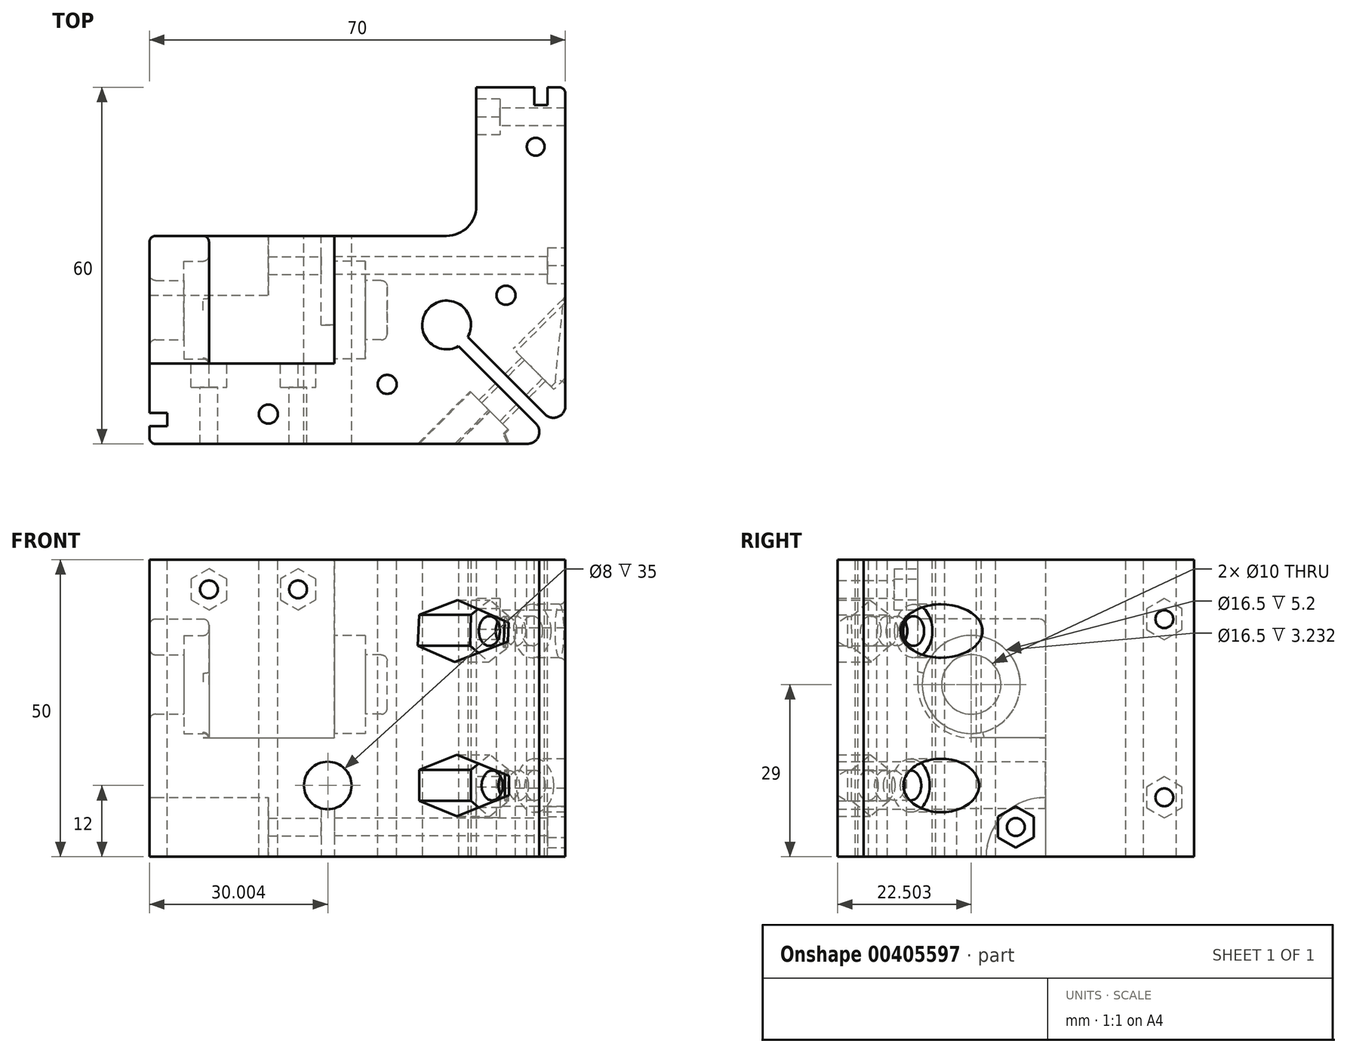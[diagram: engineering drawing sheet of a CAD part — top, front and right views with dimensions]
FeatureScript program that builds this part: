
annotation { "Feature Type Name" : "Feature", "Feature Type Description" : "" }
export const myFeature = defineFeature(function(context is Context, id is Id, definition is map)
    precondition{}
    {
        {
            var Q0;
            Q0=qCreatedBy(makeId("Top.planeOp"),FACE);
            var sketch = newSketch(context, id + "F0", { "sketchPlane" : qUnion([Q0])});
            skLineSegment(sketch, "E0.bottom", {"start": v(-61.79, 60.93) * mm, "end": v(-1.79, 60.93) * mm});
            skLineSegment(sketch, "E0.top", {"start": v(-61.79, 0.93) * mm, "end": v(-4.07, 0.93) * mm});
            skLineSegment(sketch, "E0.left", {"start": v(-61.79, 60.93) * mm, "end": v(-61.79, 0.93) * mm});
            skLineSegment(sketch, "E0.right", {"start": v(-1.79, 60.93) * mm, "end": v(-1.79, 3.21) * mm});
            skLineSegment(sketch, "E1", {"start": v(-18.22, 18.92) * mm, "end": v(-2.3, 3) * mm});
            skLineSegment(sketch, "E2.MirrorCS", {"start": v(-19.77, 17.36) * mm, "end": v(-3.85, 1.44) * mm});
            skPoint(sketch, "E3.visualSharp", {"position": v(-1.79, 2.49) * mm});
            skPoint(sketch, "E4.visualSharp", {"position": v(-3.34, 0.93) * mm});
            skArc(sketch, "E5", {"start": v(-18.22, 18.92) * mm, "mid": v(-24.69, 23.83) * mm, "end": v(-19.77, 17.36) * mm});
            skLineSegment(sketch, "E6", {"start": v(-3.85, 1.44) * mm, "end": v(-3.34, 0.93) * mm});
            skLineSegment(sketch, "E7", {"start": v(-2.3, 3) * mm, "end": v(-1.79, 2.49) * mm});
            skLineSegment(sketch, "E8", {"start": v(-1.79, 3.21) * mm, "end": v(-1.79, 2.49) * mm});
            skLineSegment(sketch, "E9", {"start": v(-3.34, 0.93) * mm, "end": v(-4.07, 0.93) * mm});
            skSolve(sketch);
        }
        {
            var Q0;
            Q0=qSketchRegion(id+"F0",true);
            extrude(context, id + "F1", {"entities" : qUnion([Q0]), "depth" : 50 * mm});
        }
        {
            var Q0;
            Q0=makeQuery(id+"F1.opExtrude","SWEPT_FACE",FACE,{"disambiguationData":[OSD([sQuery(id+"F0.wireOp",EDGE,"E1")])]});
            var sketch = newSketch(context, id + "F2", { "sketchPlane" : qUnion([Q0])});
            skCircle(sketch, "E10", {"center": v(-14.26, 12) * mm, "radius": 2.5 * mm});
            skCircle(sketch, "E11", {"center": v(-14.92, 38) * mm, "radius": 4.5 * mm});
            skCircle(sketch, "E12", {"center": v(-14.26, 12) * mm, "radius": 4.5 * mm});
            skCircle(sketch, "E13", {"center": v(-14.92, 38) * mm, "radius": 2.5 * mm});
            skCircle(sketch, "E14.cCircle", {"center": v(-14.92, 38) * mm, "radius": 4.5 * mm, "construction": true});
            skLineSegment(sketch, "E14.0", {"start": v(-10.5, 35.26) * mm, "end": v(-15.08, 32.8) * mm});
            skLineSegment(sketch, "E14.1", {"start": v(-15.08, 32.8) * mm, "end": v(-19.5, 35.54) * mm});
            skLineSegment(sketch, "E14.2", {"start": v(-19.5, 35.54) * mm, "end": v(-19.34, 40.74) * mm});
            skLineSegment(sketch, "E14.3", {"start": v(-19.34, 40.74) * mm, "end": v(-14.76, 43.2) * mm});
            skLineSegment(sketch, "E14.4", {"start": v(-14.76, 43.2) * mm, "end": v(-10.34, 40.46) * mm});
            skLineSegment(sketch, "E14.5", {"start": v(-10.34, 40.46) * mm, "end": v(-10.5, 35.26) * mm});
            skPoint(sketch, "E14.0.midPoint", {"position": v(-12.79, 34.04) * mm});
            skSolve(sketch);
        }
        {
            var Q0;
            Q0=sQuery(id+"F2.wireOp",VERTEX,"E11.center");
            var Q1;
            Q1=makeQuery(id+"F1.opExtrude","SWEPT_BODY",BODY,{"disambiguationData":[OSD([sQuery(id+"F0.wireOp",EDGE,"E0.bottom"),sQuery(id+"F0.wireOp",EDGE,"E0.top"),sQuery(id+"F0.wireOp",EDGE,"E0.left"),sQuery(id+"F0.wireOp",EDGE,"E0.right"),sQuery(id+"F0.wireOp",EDGE,"qFsGaKan-yORc-CTVH-xqod-amC7XaK1J5uG"),sQuery(id+"F0.wireOp",EDGE,"E1"),sQuery(id+"F0.wireOp",EDGE,"E2.MirrorCS"),sQuery(id+"F0.wireOp",EDGE,"cd217c19-c853-48cb-b8bd-9b78fb10cb74.filletArc"),sQuery(id+"F0.wireOp",EDGE,"a7c015ec-a513-4ea6-9d75-b2fe8166aac2.filletArc"),sQuery(id+"F0.wireOp",EDGE,"E3.filletArc"),sQuery(id+"F0.wireOp",EDGE,"E4.filletArc")])]});
            hole(context, id + "F3", {"style" : HoleStyle.SIMPLE, "endStyle" : HoleEndStyle.THROUGH, "holeDiameter" : 5 * mm, "isTappedThrough" : true, "tappedDepth" : 12 * mm, "tapClearance" : 3, "locations" : qUnion([Q0]), "scope" : qUnion([Q1])});
        }
        {
            var Q0;
            Q0=sQuery(id+"F2.wireOp",VERTEX,"E11.center");
            var Q1;
            Q1=makeQuery(id+"F1.opExtrude","SWEPT_BODY",BODY,{"disambiguationData":[OSD([sQuery(id+"F0.wireOp",EDGE,"E0.bottom"),sQuery(id+"F0.wireOp",EDGE,"E0.top"),sQuery(id+"F0.wireOp",EDGE,"E0.left"),sQuery(id+"F0.wireOp",EDGE,"E0.right"),sQuery(id+"F0.wireOp",EDGE,"qFsGaKan-yORc-CTVH-xqod-amC7XaK1J5uG"),sQuery(id+"F0.wireOp",EDGE,"E1"),sQuery(id+"F0.wireOp",EDGE,"E2.MirrorCS"),sQuery(id+"F0.wireOp",EDGE,"cd217c19-c853-48cb-b8bd-9b78fb10cb74.filletArc"),sQuery(id+"F0.wireOp",EDGE,"a7c015ec-a513-4ea6-9d75-b2fe8166aac2.filletArc"),sQuery(id+"F0.wireOp",EDGE,"E3.filletArc"),sQuery(id+"F0.wireOp",EDGE,"E4.filletArc")])]});
            hole(context, id + "F4", {"style" : HoleStyle.SIMPLE, "endStyle" : HoleEndStyle.THROUGH, "oppositeDirection" : true, "standardTappedOrClearance" : lookupTablePath({ "standard" : "自訂" }), "standardBlindInLast" : lookupTablePath({ "standard" : "自訂" }), "holeDiameter" : 5 * mm, "isTappedThrough" : true, "tappedDepth" : 12 * mm, "tapClearance" : 3, "locations" : qUnion([Q0]), "scope" : qUnion([Q1])});
        }
        {
            var Q0;
            Q0=makeQuery(id+"F2.imprint","IMPRINT",FACE,{"disambiguationData":[TD([[makeQuery(id+"F2.imprint","IMPRINT",EDGE,{"derivedFrom":sQuery(id+"F2.wireOp",EDGE,"E11")}),1.0]])]});
            var Q1;
            Q1=sQuery(id+"F2.wireOp",EDGE,"E11");
            extrude(context, id + "F5", {"entities" : qUnion([Q0]), "surfaceEntities" : qUnion([Q1]), "oppositeDirection" : true, "depth" : 25 * mm});
        }
        {
            var Q0;
            Q0=makeQuery(id+"F5.opExtrude","SWEPT_BODY",BODY,{"disambiguationData":[OSD([sQuery(id+"F2.wireOp",EDGE,"E11"),sQuery(id+"F2.wireOp",EDGE,"E13")])]});
            var Q1;
            Q1=makeQuery(id+"F1.opExtrude","SWEPT_BODY",BODY,{"disambiguationData":[OSD([sQuery(id+"F0.wireOp",EDGE,"E0.bottom"),sQuery(id+"F0.wireOp",EDGE,"E0.top"),sQuery(id+"F0.wireOp",EDGE,"E0.left"),sQuery(id+"F0.wireOp",EDGE,"E0.right"),sQuery(id+"F0.wireOp",EDGE,"qFsGaKan-yORc-CTVH-xqod-amC7XaK1J5uG"),sQuery(id+"F0.wireOp",EDGE,"E1"),sQuery(id+"F0.wireOp",EDGE,"E2.MirrorCS"),sQuery(id+"F0.wireOp",EDGE,"cd217c19-c853-48cb-b8bd-9b78fb10cb74.filletArc"),sQuery(id+"F0.wireOp",EDGE,"a7c015ec-a513-4ea6-9d75-b2fe8166aac2.filletArc"),sQuery(id+"F0.wireOp",EDGE,"E3.filletArc"),sQuery(id+"F0.wireOp",EDGE,"E4.filletArc")])]});
            booleanBodies(context, id + "F6", {"operationType" : BooleanOperationType.SUBTRACTION, "tools" : qUnion([Q0]), "targets" : qUnion([Q1])});
        }
        {
            var Q0;
            Q0=makeQuery(id+"F2.imprint","IMPRINT",FACE,{"disambiguationData":[TD([[makeQuery(id+"F2.imprint","IMPRINT",EDGE,{"derivedFrom":sQuery(id+"F2.wireOp",EDGE,"E11")}),1.0]])]});
            extrude(context, id + "F7", {"entities" : qUnion([Q0]), "operationType" : NewBodyOperationType.ADD, "oppositeDirection" : true, "depth" : 4 * mm});
        }
        {
            var Q0;
            Q0=sQuery(id+"F2.wireOp",VERTEX,"E10.center");
            var Q1;
            Q1=makeQuery(id+"F1.opExtrude","SWEPT_BODY",BODY,{"disambiguationData":[OSD([sQuery(id+"F0.wireOp",EDGE,"E0.bottom"),sQuery(id+"F0.wireOp",EDGE,"E0.top"),sQuery(id+"F0.wireOp",EDGE,"E0.left"),sQuery(id+"F0.wireOp",EDGE,"E0.right"),sQuery(id+"F0.wireOp",EDGE,"qFsGaKan-yORc-CTVH-xqod-amC7XaK1J5uG"),sQuery(id+"F0.wireOp",EDGE,"E1"),sQuery(id+"F0.wireOp",EDGE,"E2.MirrorCS"),sQuery(id+"F0.wireOp",EDGE,"cd217c19-c853-48cb-b8bd-9b78fb10cb74.filletArc"),sQuery(id+"F0.wireOp",EDGE,"a7c015ec-a513-4ea6-9d75-b2fe8166aac2.filletArc"),sQuery(id+"F0.wireOp",EDGE,"E3.filletArc"),sQuery(id+"F0.wireOp",EDGE,"E4.filletArc")])]});
            hole(context, id + "F8", {"style" : HoleStyle.SIMPLE, "endStyle" : HoleEndStyle.THROUGH, "oppositeDirection" : true, "standardTappedOrClearance" : lookupTablePath({ "standard" : "自訂" }), "standardBlindInLast" : lookupTablePath({ "standard" : "自訂" }), "holeDiameter" : 5 * mm, "isTappedThrough" : true, "tappedDepth" : 12 * mm, "tapClearance" : 3, "locations" : qUnion([Q0]), "scope" : qUnion([Q1])});
        }
        {
            var Q0;
            Q0=makeQuery(id+"F1.opExtrude","SWEPT_FACE",FACE,{"disambiguationData":[OSD([sQuery(id+"F0.wireOp",EDGE,"E2.MirrorCS")])]});
            var sketch = newSketch(context, id + "F9", { "sketchPlane" : qUnion([Q0])});
            skCircle(sketch, "E15.cCircle", {"center": v(14.92, 38) * mm, "radius": 4.5 * mm, "construction": true});
            skLineSegment(sketch, "E15.0", {"start": v(10.34, 40.45) * mm, "end": v(14.75, 43.2) * mm});
            skLineSegment(sketch, "E15.1", {"start": v(14.75, 43.2) * mm, "end": v(19.33, 40.74) * mm});
            skLineSegment(sketch, "E15.2", {"start": v(19.33, 40.74) * mm, "end": v(19.5, 35.55) * mm});
            skLineSegment(sketch, "E15.3", {"start": v(19.5, 35.55) * mm, "end": v(15.08, 32.8) * mm});
            skLineSegment(sketch, "E15.4", {"start": v(15.08, 32.8) * mm, "end": v(10.5, 35.26) * mm});
            skLineSegment(sketch, "E15.5", {"start": v(10.5, 35.26) * mm, "end": v(10.34, 40.45) * mm});
            skPoint(sketch, "E15.0.midPoint", {"position": v(12.54, 41.82) * mm});
            skCircle(sketch, "E16", {"center": v(14.92, 38) * mm, "radius": 2.5 * mm});
            skCircle(sketch, "E17.cCircle", {"center": v(14.82, 12) * mm, "radius": 4.5 * mm, "construction": true});
            skLineSegment(sketch, "E17.0", {"start": v(19.32, 14.6) * mm, "end": v(19.32, 9.4) * mm});
            skLineSegment(sketch, "E17.1", {"start": v(19.32, 9.4) * mm, "end": v(14.82, 6.8) * mm});
            skLineSegment(sketch, "E17.2", {"start": v(14.82, 6.8) * mm, "end": v(10.32, 9.4) * mm});
            skLineSegment(sketch, "E17.3", {"start": v(10.32, 9.4) * mm, "end": v(10.32, 14.6) * mm});
            skLineSegment(sketch, "E17.4", {"start": v(10.32, 14.6) * mm, "end": v(14.82, 17.2) * mm});
            skLineSegment(sketch, "E17.5", {"start": v(14.82, 17.2) * mm, "end": v(19.32, 14.6) * mm});
            skPoint(sketch, "E17.0.midPoint", {"position": v(19.32, 12) * mm});
            skSolve(sketch);
        }
        {
            var Q0;
            Q0=qSketchRegion(id+"F9",true);
            extrude(context, id + "F10", {"entities" : qUnion([Q0]), "operationType" : NewBodyOperationType.REMOVE, "oppositeDirection" : true, "depth" : 25 * mm});
        }
        {
            var Q0;
            Q0=makeQuery(id+"F9.imprint","IMPRINT",FACE,{"disambiguationData":[TD([[makeQuery(id+"F9.imprint","IMPRINT",EDGE,{"derivedFrom":sQuery(id+"F9.wireOp",EDGE,"E15.0")}),-1.0]])]});
            var Q1;
            Q1=sQuery(id+"F9.wireOp",EDGE,"E15.2");
            extrude(context, id + "F11", {"entities" : qUnion([Q0]), "operationType" : NewBodyOperationType.ADD, "surfaceEntities" : qUnion([Q1]), "oppositeDirection" : true, "depth" : 4 * mm});
        }
        {
            var Q0;
            Q0=sQuery(id+"F2.wireOp",VERTEX,"E10.center");
            var Q1;
            Q1=makeQuery(id+"F1.opExtrude","SWEPT_BODY",BODY,{"disambiguationData":[OSD([sQuery(id+"F0.wireOp",EDGE,"E0.bottom"),sQuery(id+"F0.wireOp",EDGE,"E0.top"),sQuery(id+"F0.wireOp",EDGE,"E0.left"),sQuery(id+"F0.wireOp",EDGE,"E0.right"),sQuery(id+"F0.wireOp",EDGE,"qFsGaKan-yORc-CTVH-xqod-amC7XaK1J5uG"),sQuery(id+"F0.wireOp",EDGE,"E1"),sQuery(id+"F0.wireOp",EDGE,"E2.MirrorCS"),sQuery(id+"F0.wireOp",EDGE,"cd217c19-c853-48cb-b8bd-9b78fb10cb74.filletArc"),sQuery(id+"F0.wireOp",EDGE,"a7c015ec-a513-4ea6-9d75-b2fe8166aac2.filletArc"),sQuery(id+"F0.wireOp",EDGE,"E3.filletArc"),sQuery(id+"F0.wireOp",EDGE,"E4.filletArc")])]});
            hole(context, id + "F12", {"style" : HoleStyle.SIMPLE, "endStyle" : HoleEndStyle.THROUGH, "standardTappedOrClearance" : lookupTablePath({ "standard" : "自訂" }), "standardBlindInLast" : lookupTablePath({ "standard" : "自訂" }), "holeDiameter" : 9 * mm, "isTappedThrough" : true, "tappedDepth" : 12 * mm, "tapClearance" : 3, "locations" : qUnion([Q0]), "scope" : qUnion([Q1])});
        }
        {
            var Q0;
            Q0=makeQuery(id+"F2.imprint","IMPRINT",FACE,{"disambiguationData":[TD([[makeQuery(id+"F2.imprint","IMPRINT",EDGE,{"derivedFrom":sQuery(id+"F2.wireOp",EDGE,"E10")}),-1.0]])]});
            extrude(context, id + "F13", {"entities" : qUnion([Q0]), "operationType" : NewBodyOperationType.ADD, "oppositeDirection" : true, "depth" : 4 * mm});
        }
        {
            var Q0;
            Q0=makeQuery(id+"F9.imprint","IMPRINT",FACE,{"disambiguationData":[TD([[makeQuery(id+"F9.imprint","IMPRINT",EDGE,{"derivedFrom":sQuery(id+"F9.wireOp",EDGE,"E17.0")}),-1.0]])]});
            extrude(context, id + "F14", {"entities" : qUnion([Q0]), "operationType" : NewBodyOperationType.ADD, "oppositeDirection" : true, "depth" : 4 * mm});
        }
        {
            var Q0;
            Q0=makeQuery(id+"F1.opExtrude","SWEPT_FACE",FACE,{"disambiguationData":[OSD([sQuery(id+"F0.wireOp",EDGE,"E0.bottom")])]});
            var sketch = newSketch(context, id + "F15", { "sketchPlane" : qUnion([Q0])});
            skCircle(sketch, "E18", {"center": v(41.79, 12) * mm, "radius": 1.1 * mm});
            skLineSegment(sketch, "E19", {"start": v(40.69, 50) * mm, "end": v(40.69, 0) * mm});
            skLineSegment(sketch, "E20.MirrorCS", {"start": v(42.89, 50) * mm, "end": v(42.89, 0) * mm});
            skLineSegment(sketch, "E21", {"start": v(16.79, 50) * mm, "end": v(16.79, 0) * mm});
            skLineSegment(sketch, "E22.bottom", {"start": v(40.69, 50) * mm, "end": v(42.89, 50) * mm});
            skLineSegment(sketch, "E22.left", {"start": v(40.69, 50) * mm, "end": v(40.69, 30) * mm});
            skSolve(sketch);
        }
        {
            var Q0;
            Q0=sQuery(id+"F15.wireOp",VERTEX,"E18.center");
            var Q1;
            Q1=makeQuery(id+"F1.opExtrude","SWEPT_BODY",BODY,{"disambiguationData":[OSD([sQuery(id+"F0.wireOp",EDGE,"E0.bottom"),sQuery(id+"F0.wireOp",EDGE,"E0.top"),sQuery(id+"F0.wireOp",EDGE,"E0.left"),sQuery(id+"F0.wireOp",EDGE,"E0.right"),sQuery(id+"F0.wireOp",EDGE,"qFsGaKan-yORc-CTVH-xqod-amC7XaK1J5uG"),sQuery(id+"F0.wireOp",EDGE,"E1"),sQuery(id+"F0.wireOp",EDGE,"E2.MirrorCS"),sQuery(id+"F0.wireOp",EDGE,"cd217c19-c853-48cb-b8bd-9b78fb10cb74.filletArc"),sQuery(id+"F0.wireOp",EDGE,"a7c015ec-a513-4ea6-9d75-b2fe8166aac2.filletArc"),sQuery(id+"F0.wireOp",EDGE,"E3.filletArc"),sQuery(id+"F0.wireOp",EDGE,"E4.filletArc")])]});
            hole(context, id + "F16", {"style" : HoleStyle.SIMPLE, "endStyle" : HoleEndStyle.THROUGH, "standardTappedOrClearance" : lookupTablePath({ "standard" : "自訂" }), "standardBlindInLast" : lookupTablePath({ "standard" : "自訂" }), "holeDiameter" : 8 * mm, "isTappedThrough" : true, "tappedDepth" : 12 * mm, "tapClearance" : 3, "locations" : qUnion([Q0]), "scope" : qUnion([Q1])});
        }
        {
            var Q0;
            {var subQ0=sQuery(id+"F15.wireOp",EDGE,"E19");var subQ1=sQuery(id+"F15.wireOp",EDGE,"E18");var subQ2=makeQuery(id+"F15.imprint","INTERSECT",VERTEX,{"derivedFrom":[subQ1,subQ0]});Q0=makeQuery(id+"F15.imprint","IMPRINT",FACE,{"disambiguationData":[TD([[makeQuery(id+"F15.imprint","IMPRINT",EDGE,{"disambiguationData":[TD([[subQ2,-1.0]])],"derivedFrom":subQ1}),-1.0]])]});}
            extrude(context, id + "F17", {"entities" : qUnion([Q0]), "operationType" : NewBodyOperationType.REMOVE, "oppositeDirection" : true, "depth" : 40 * mm});
        }
        {
            var Q0;
            Q0=makeQuery(id+"F1.opExtrude","SWEPT_BODY",BODY,{"disambiguationData":[OSD([sQuery(id+"F0.wireOp",EDGE,"E0.bottom"),sQuery(id+"F0.wireOp",EDGE,"E0.top"),sQuery(id+"F0.wireOp",EDGE,"E0.left"),sQuery(id+"F0.wireOp",EDGE,"E0.right"),sQuery(id+"F0.wireOp",EDGE,"qFsGaKan-yORc-CTVH-xqod-amC7XaK1J5uG"),sQuery(id+"F0.wireOp",EDGE,"E1"),sQuery(id+"F0.wireOp",EDGE,"E2.MirrorCS"),sQuery(id+"F0.wireOp",EDGE,"cd217c19-c853-48cb-b8bd-9b78fb10cb74.filletArc"),sQuery(id+"F0.wireOp",EDGE,"a7c015ec-a513-4ea6-9d75-b2fe8166aac2.filletArc"),sQuery(id+"F0.wireOp",EDGE,"E3.filletArc"),sQuery(id+"F0.wireOp",EDGE,"E4.filletArc")])]});
            var Q1;
            Q1=qCreatedBy(makeId("Right.planeOp"),FACE);
            mirror(context, id + "F18", {"entities" : qUnion([Q0]), "mirrorPlane" : qUnion([Q1])});
        }
        {
            var Q0;
            Q0=makeQuery(id+"F1.opExtrude","CAP_FACE",FACE,{"disambiguationData":[OSD([sQuery(id+"F0.wireOp",EDGE,"E0.bottom"),sQuery(id+"F0.wireOp",EDGE,"E0.top"),sQuery(id+"F0.wireOp",EDGE,"E0.left"),sQuery(id+"F0.wireOp",EDGE,"E0.right"),sQuery(id+"F0.wireOp",EDGE,"qFsGaKan-yORc-CTVH-xqod-amC7XaK1J5uG"),sQuery(id+"F0.wireOp",EDGE,"E1"),sQuery(id+"F0.wireOp",EDGE,"E2.MirrorCS"),sQuery(id+"F0.wireOp",EDGE,"cd217c19-c853-48cb-b8bd-9b78fb10cb74.filletArc"),sQuery(id+"F0.wireOp",EDGE,"a7c015ec-a513-4ea6-9d75-b2fe8166aac2.filletArc"),sQuery(id+"F0.wireOp",EDGE,"E3.filletArc"),sQuery(id+"F0.wireOp",EDGE,"E4.filletArc")])],"isStart":false});
            var sketch = newSketch(context, id + "F19", { "sketchPlane" : qUnion([Q0])});
            skCircle(sketch, "E23", {"center": v(-51.79, 5.93) * mm, "radius": 1.6 * mm});
            skCircle(sketch, "E24", {"center": v(-6.79, 50.93) * mm, "radius": 1.5 * mm});
            skCircle(sketch, "E25", {"center": v(-11.79, 25.93) * mm, "radius": 1.6 * mm});
            skCircle(sketch, "E26", {"center": v(-31.79, 10.93) * mm, "radius": 1.6 * mm});
            skSolve(sketch);
        }
        {
            var Q0;
            {var subQ0=sQuery(id+"F15.wireOp",EDGE,"E21");Q0=makeQuery(id+"F15.imprint","IMPRINT",FACE,{"disambiguationData":[TD([[makeQuery(id+"F15.imprint","IMPRINT",EDGE,{"derivedFrom":subQ0}),1.0]])]});}
            var Q1;
            {var subQ0=sQuery(id+"F0.wireOp",EDGE,"E0.bottom");var subQ1=makeQuery(id+"F1.opExtrude","SWEPT_EDGE",EDGE,{"disambiguationData":[OSD([subQ0,sQuery(id+"F0.wireOp",EDGE,"E0.left")])]});Q1=makeQuery(id+"F15.imprint","IMPRINT",FACE,{"disambiguationData":[TD([[makeQuery(id+"F15.imprint","IMPRINT",EDGE,{"derivedFrom":subQ1}),-1.0]])]});}
            var Q2;
            {var subQ0=sQuery(id+"F15.wireOp",EDGE,"E22.bottom");Q2=makeQuery(id+"F15.imprint","IMPRINT",FACE,{"disambiguationData":[TD([[makeQuery(id+"F15.imprint","IMPRINT",EDGE,{"derivedFrom":subQ0}),1.0]])]});}
            extrude(context, id + "F20", {"entities" : qUnion([Q0, Q1, Q2]), "operationType" : NewBodyOperationType.REMOVE, "oppositeDirection" : true, "depth" : 25 * mm});
        }
        {
            var Q0;
            Q0=qSketchRegion(id+"F19",true);
            extrude(context, id + "F21", {"entities" : qUnion([Q0]), "operationType" : NewBodyOperationType.REMOVE, "endBound" : BoundingType.THROUGH_ALL, "oppositeDirection" : true, "depth" : 25 * mm});
        }
        {
            var Q0;
            {var subQ0=sQuery(id+"F15.wireOp",EDGE,"E22.left");var subQ1=sQuery(id+"F15.wireOp",EDGE,"E19");Q0=makeQuery(id+"FdHSFXm388vhnnI_1.boolean.opBoolean","MERGE",FACE,{"derivedFrom":[makeQuery(id+"F17.boolean.opBoolean","COPY",FACE,{"derivedFrom":makeQuery(id+"F17.opExtrude","SWEPT_FACE",FACE,{"disambiguationData":[OSD([subQ1]),TDD([makeQuery(id+"F15.imprint","IMPRINT",EDGE,{"disambiguationData":[TD([[makeQuery(id+"F15.imprint","INTERSECT",VERTEX,{"derivedFrom":[sQuery(id+"F15.wireOp",EDGE,"E18"),subQ1]}),1.0]])],"derivedFrom":subQ1})])]})}),makeQuery(id+"FdHSFXm388vhnnI_1.opExtrude","SWEPT_FACE",FACE,{"disambiguationData":[OSD([subQ1,subQ0])]})]});}
            var sketch = newSketch(context, id + "F22", { "sketchPlane" : qUnion([Q0])});
            skCircle(sketch, "E27", {"center": v(-30.93, 5) * mm, "radius": 1.5 * mm});
            skCircle(sketch, "E28", {"center": v(-23.43, 29) * mm, "radius": 8.25 * mm});
            skArc(sketch, "E29", {"start": v(-23.43, 20) * mm, "mid": v(-17.07, 22.64) * mm, "end": v(-14.43, 29) * mm});
            skLineSegment(sketch, "E30", {"start": v(-35.93, 20) * mm, "end": v(-23.43, 20) * mm});
            skLineSegment(sketch, "E31", {"start": v(-35.93, 38) * mm, "end": v(-35.93, 20) * mm});
            skCircle(sketch, "E32", {"center": v(-23.43, 29) * mm, "radius": 5 * mm});
            skLineSegment(sketch, "E33", {"start": v(-14.43, 29) * mm, "end": v(-14.43, 54.02) * mm});
            skLineSegment(sketch, "E34", {"start": v(-14.43, 54.02) * mm, "end": v(-35.93, 54.02) * mm});
            skLineSegment(sketch, "E35", {"start": v(-35.93, 54.02) * mm, "end": v(-35.93, 38) * mm});
            skSolve(sketch);
        }
        {
            var Q0;
            Q0=sQuery(id+"F22.wireOp",VERTEX,"zC7tOIGd-IPTA-Gwrh-6AtB-gp47nifF0IhA.center");
            var Q1;
            Q1=sQuery(id+"F22.wireOp",VERTEX,"E27.center");
            var Q2;
            Q2=makeQuery(id+"F1.opExtrude","SWEPT_BODY",BODY,{"disambiguationData":[OSD([sQuery(id+"F0.wireOp",EDGE,"E0.bottom"),sQuery(id+"F0.wireOp",EDGE,"E0.top"),sQuery(id+"F0.wireOp",EDGE,"E0.left"),sQuery(id+"F0.wireOp",EDGE,"E0.right"),sQuery(id+"F0.wireOp",EDGE,"qFsGaKan-yORc-CTVH-xqod-amC7XaK1J5uG"),sQuery(id+"F0.wireOp",EDGE,"E1"),sQuery(id+"F0.wireOp",EDGE,"E2.MirrorCS"),sQuery(id+"F0.wireOp",EDGE,"cd217c19-c853-48cb-b8bd-9b78fb10cb74.filletArc"),sQuery(id+"F0.wireOp",EDGE,"a7c015ec-a513-4ea6-9d75-b2fe8166aac2.filletArc"),sQuery(id+"F0.wireOp",EDGE,"E3.filletArc"),sQuery(id+"F0.wireOp",EDGE,"E4.filletArc")])]});
            hole(context, id + "F23", {"style" : HoleStyle.SIMPLE, "endStyle" : HoleEndStyle.THROUGH, "standardTappedOrClearance" : lookupTablePath({ "standard" : "自訂" }), "standardBlindInLast" : lookupTablePath({ "standard" : "自訂" }), "holeDiameter" : 3 * mm, "isTappedThrough" : true, "tappedDepth" : 12 * mm, "tapClearance" : 3, "locations" : qUnion([Q0, Q1]), "scope" : qUnion([Q2])});
        }
        {
            var Q0;
            Q0=qCreatedBy(makeId("Right.planeOp"),FACE);
            cPlane(context, id + "F24", {"entities" : qUnion([Q0]), "cplaneType" : CPlaneType.OFFSET, "offset" : 70 * mm, "oppositeDirection" : true, "width" : 150 * mm, "height" : 150 * mm});
        }
        {
            var Q0;
            Q0=makeQuery(id+"F1.opExtrude","SWEPT_FACE",FACE,{"disambiguationData":[OSD([sQuery(id+"F0.wireOp",EDGE,"E0.right")])]});
            var sketch = newSketch(context, id + "F25", { "sketchPlane" : qUnion([Q0])});
            skCircle(sketch, "E36.cCircle", {"center": v(30.93, 5) * mm, "radius": 3 * mm, "construction": true});
            skLineSegment(sketch, "E36.0", {"start": v(33.93, 3.27) * mm, "end": v(30.93, 1.54) * mm});
            skLineSegment(sketch, "E36.1", {"start": v(30.93, 1.54) * mm, "end": v(27.93, 3.27) * mm});
            skLineSegment(sketch, "E36.2", {"start": v(27.93, 3.27) * mm, "end": v(27.93, 6.73) * mm});
            skLineSegment(sketch, "E36.3", {"start": v(27.93, 6.73) * mm, "end": v(30.93, 8.46) * mm});
            skLineSegment(sketch, "E36.4", {"start": v(30.93, 8.46) * mm, "end": v(33.93, 6.73) * mm});
            skLineSegment(sketch, "E36.5", {"start": v(33.93, 6.73) * mm, "end": v(33.93, 3.27) * mm});
            skPoint(sketch, "E36.0.midPoint", {"position": v(32.43, 2.4) * mm});
            skSolve(sketch);
        }
        {
            var Q0;
            Q0=makeQuery(id+"F22.imprint","IMPRINT",FACE,{"disambiguationData":[TD([[makeQuery(id+"F22.imprint","IMPRINT",EDGE,{"derivedFrom":sQuery(id+"F22.wireOp",EDGE,"E28")}),-1.0]])]});
            var Q1;
            Q1=makeQuery(id+"F22.imprint","IMPRINT",FACE,{"disambiguationData":[TD([[makeQuery(id+"F22.imprint","IMPRINT",EDGE,{"derivedFrom":sQuery(id+"F22.wireOp",EDGE,"E28")}),1.0]])]});
            var Q2;
            Q2=makeQuery(id+"F22.imprint","IMPRINT",FACE,{"disambiguationData":[TD([[makeQuery(id+"F22.imprint","IMPRINT",EDGE,{"derivedFrom":sQuery(id+"F22.wireOp",EDGE,"PrOkHBf4-ZMx0-2PIS-lLmz-FP7QmJ8HfarF")}),1.0]])]});
            extrude(context, id + "F26", {"entities" : qUnion([Q0, Q1, Q2]), "operationType" : NewBodyOperationType.REMOVE, "depth" : 25 * mm});
        }
        {
            var Q0;
            Q0=qSketchRegion(id+"F25",true);
            extrude(context, id + "F27", {"entities" : qUnion([Q0]), "operationType" : NewBodyOperationType.REMOVE, "oppositeDirection" : true, "depth" : 3 * mm});
        }
        {
            var Q0;
            Q0=makeQuery(id+"F1.opExtrude","SWEPT_BODY",BODY,{"disambiguationData":[OSD([sQuery(id+"F0.wireOp",EDGE,"E0.bottom"),sQuery(id+"F0.wireOp",EDGE,"E0.top"),sQuery(id+"F0.wireOp",EDGE,"E0.left"),sQuery(id+"F0.wireOp",EDGE,"E0.right"),sQuery(id+"F0.wireOp",EDGE,"qFsGaKan-yORc-CTVH-xqod-amC7XaK1J5uG"),sQuery(id+"F0.wireOp",EDGE,"E1"),sQuery(id+"F0.wireOp",EDGE,"E2.MirrorCS"),sQuery(id+"F0.wireOp",EDGE,"cd217c19-c853-48cb-b8bd-9b78fb10cb74.filletArc"),sQuery(id+"F0.wireOp",EDGE,"a7c015ec-a513-4ea6-9d75-b2fe8166aac2.filletArc"),sQuery(id+"F0.wireOp",EDGE,"E3.filletArc"),sQuery(id+"F0.wireOp",EDGE,"E4.filletArc")])]});
            var Q1;
            Q1=qCreatedBy(id+"F24.planeOp",FACE);
            mirror(context, id + "F28", {"entities" : qUnion([Q0]), "mirrorPlane" : qUnion([Q1])});
        }
        {
            var Q0;
            Q0=makeQuery(id+"F22.imprint","IMPRINT",FACE,{"disambiguationData":[TD([[makeQuery(id+"F22.imprint","IMPRINT",EDGE,{"derivedFrom":sQuery(id+"F22.wireOp",EDGE,"E28")}),1.0]])]});
            extrude(context, id + "F29", {"entities" : qUnion([Q0]), "operationType" : NewBodyOperationType.REMOVE, "oppositeDirection" : true, "depth" : 5.2 * mm});
        }
        {
            var Q0;
            Q0=makeQuery(id+"F28.opPattern","COPY",BODY,{"derivedFrom":makeQuery(id+"F1.opExtrude","SWEPT_BODY",BODY,{"disambiguationData":[OSD([sQuery(id+"F0.wireOp",EDGE,"E0.bottom"),sQuery(id+"F0.wireOp",EDGE,"E0.top"),sQuery(id+"F0.wireOp",EDGE,"E0.left"),sQuery(id+"F0.wireOp",EDGE,"E0.right"),sQuery(id+"F0.wireOp",EDGE,"qFsGaKan-yORc-CTVH-xqod-amC7XaK1J5uG"),sQuery(id+"F0.wireOp",EDGE,"E1"),sQuery(id+"F0.wireOp",EDGE,"E2.MirrorCS"),sQuery(id+"F0.wireOp",EDGE,"cd217c19-c853-48cb-b8bd-9b78fb10cb74.filletArc"),sQuery(id+"F0.wireOp",EDGE,"a7c015ec-a513-4ea6-9d75-b2fe8166aac2.filletArc"),sQuery(id+"F0.wireOp",EDGE,"E3.filletArc"),sQuery(id+"F0.wireOp",EDGE,"E4.filletArc")])]}),"instanceName":"1"});
            var Q1;
            Q1=makeQuery(id+"F18.opPattern","COPY",BODY,{"derivedFrom":makeQuery(id+"F1.opExtrude","SWEPT_BODY",BODY,{"disambiguationData":[OSD([sQuery(id+"F0.wireOp",EDGE,"E0.bottom"),sQuery(id+"F0.wireOp",EDGE,"E0.top"),sQuery(id+"F0.wireOp",EDGE,"E0.left"),sQuery(id+"F0.wireOp",EDGE,"E0.right"),sQuery(id+"F0.wireOp",EDGE,"qFsGaKan-yORc-CTVH-xqod-amC7XaK1J5uG"),sQuery(id+"F0.wireOp",EDGE,"E1"),sQuery(id+"F0.wireOp",EDGE,"E2.MirrorCS"),sQuery(id+"F0.wireOp",EDGE,"cd217c19-c853-48cb-b8bd-9b78fb10cb74.filletArc"),sQuery(id+"F0.wireOp",EDGE,"a7c015ec-a513-4ea6-9d75-b2fe8166aac2.filletArc"),sQuery(id+"F0.wireOp",EDGE,"E3.filletArc"),sQuery(id+"F0.wireOp",EDGE,"E4.filletArc")])]}),"instanceName":"1"});
            deleteBodies(context, id + "F30", {"entities" : qUnion([Q0, Q1])});
        }
        {
            var Q0;
            Q0=makeQuery(id+"F26.boolean.opBoolean","SPLIT",FACE,{"disambiguationData":[TD([makeQuery(id+"F26.opExtrude","SWEPT_FACE",FACE,{"disambiguationData":[OSD([sQuery(id+"F22.wireOp",EDGE,"E32")])]})])],"derivedFrom":makeQuery(id+"F1.opExtrude","SWEPT_FACE",FACE,{"disambiguationData":[OSD([sQuery(id+"F0.wireOp",EDGE,"E0.left")])]})});
            extrude(context, id + "F31", {"entities" : qUnion([Q0]), "operationType" : NewBodyOperationType.REMOVE, "oppositeDirection" : true, "depth" : 30 * mm});
        }
        {
            var Q0;
            {var subQ0=sQuery(id+"F0.wireOp",EDGE,"E0.top");var subQ9=sQuery(id+"F0.wireOp",EDGE,"E0.left");Q0=makeQuery(id+"F26.boolean.opBoolean","SPLIT",FACE,{"disambiguationData":[TD([makeQuery(id+"F1.opExtrude","SWEPT_FACE",FACE,{"disambiguationData":[OSD([subQ0])]})])],"derivedFrom":makeQuery(id+"F1.opExtrude","SWEPT_FACE",FACE,{"disambiguationData":[OSD([subQ9])]})});}
            var sketch = newSketch(context, id + "F32", { "sketchPlane" : qUnion([Q0])});
            skLineSegment(sketch, "E37.bottom", {"start": v(-14.43, 50) * mm, "end": v(-0.93, 50) * mm});
            skLineSegment(sketch, "E37.top", {"start": v(-35.93, 0) * mm, "end": v(-0.93, 0) * mm});
            skLineSegment(sketch, "E37.left", {"start": v(-35.93, 40) * mm, "end": v(-35.93, 0) * mm});
            skLineSegment(sketch, "E37.right", {"start": v(-0.93, 50) * mm, "end": v(-0.93, 0) * mm});
            skLineSegment(sketch, "E38", {"start": v(-35.93, 40) * mm, "end": v(-14.43, 40) * mm});
            skPoint(sketch, "E38.endSnap0", {"position": v(-14.43, 39.5) * mm});
            skLineSegment(sketch, "E39", {"start": v(-14.43, 39.5) * mm, "end": v(-14.43, 50) * mm});
            skLineSegment(sketch, "E40.bottom", {"start": v(-35.93, 0) * mm, "end": v(-25.93, 0) * mm});
            skLineSegment(sketch, "E40.left", {"start": v(-35.93, 0) * mm, "end": v(-35.93, 10) * mm});
            skLineSegment(sketch, "E40.right", {"start": v(-25.93, 0) * mm, "end": v(-25.93, 10) * mm});
            skLineSegment(sketch, "E41", {"start": v(-33.93, 10) * mm, "end": v(-25.93, 10) * mm});
            skLineSegment(sketch, "E42", {"start": v(-33.93, 10) * mm, "end": v(-35.93, 10) * mm});
            skSolve(sketch);
        }
        {
            var Q0;
            Q0=qSketchRegion(id+"F32",true);
            extrude(context, id + "F33", {"entities" : qUnion([Q0]), "operationType" : NewBodyOperationType.ADD, "depth" : 10 * mm});
        }
        {
            var Q0;
            Q0=makeQuery(id+"F29.boolean.opBoolean","COPY",FACE,{"derivedFrom":makeQuery(id+"F29.opExtrude","CAP_FACE",FACE,{"disambiguationData":[OSD([sQuery(id+"F22.wireOp",EDGE,"E28"),sQuery(id+"F22.wireOp",EDGE,"E32")])],"isStart":false})});
            var Q1;
            Q1=sQuery(id+"F22.wireOp",EDGE,"E28");
            extrude(context, id + "F34", {"entities" : qUnion([Q0]), "operationType" : NewBodyOperationType.REMOVE, "surfaceEntities" : qUnion([Q1]), "depth" : 30.5 * mm});
        }
        {
            var Q0;
            Q0=makeQuery(id+"F31.boolean.opBoolean","COPY",FACE,{"derivedFrom":makeQuery(id+"F31.opExtrude","CAP_FACE",FACE,{"disambiguationData":[OSD([sQuery(id+"F0.wireOp",EDGE,"E0.left")])],"isStart":false})});
            extrude(context, id + "F35", {"entities" : qUnion([Q0]), "operationType" : NewBodyOperationType.REMOVE, "endBound" : BoundingType.THROUGH_ALL, "depth" : 25 * mm});
        }
        {
            var Q0;
            Q0=sQuery(id+"F22.wireOp",VERTEX,"zC7tOIGd-IPTA-Gwrh-6AtB-gp47nifF0IhA.center");
            var Q1;
            Q1=sQuery(id+"F22.wireOp",VERTEX,"E27.center");
            var Q2;
            Q2=makeQuery(id+"F1.opExtrude","SWEPT_BODY",BODY,{"disambiguationData":[OSD([sQuery(id+"F0.wireOp",EDGE,"E0.bottom"),sQuery(id+"F0.wireOp",EDGE,"E0.top"),sQuery(id+"F0.wireOp",EDGE,"E0.left"),sQuery(id+"F0.wireOp",EDGE,"E0.right"),sQuery(id+"F0.wireOp",EDGE,"qFsGaKan-yORc-CTVH-xqod-amC7XaK1J5uG"),sQuery(id+"F0.wireOp",EDGE,"E1"),sQuery(id+"F0.wireOp",EDGE,"E2.MirrorCS"),sQuery(id+"F0.wireOp",EDGE,"cd217c19-c853-48cb-b8bd-9b78fb10cb74.filletArc"),sQuery(id+"F0.wireOp",EDGE,"a7c015ec-a513-4ea6-9d75-b2fe8166aac2.filletArc"),sQuery(id+"F0.wireOp",EDGE,"E3.filletArc"),sQuery(id+"F0.wireOp",EDGE,"E4.filletArc")])]});
            hole(context, id + "F36", {"style" : HoleStyle.SIMPLE, "endStyle" : HoleEndStyle.THROUGH, "oppositeDirection" : true, "standardTappedOrClearance" : lookupTablePath({ "standard" : "自訂" }), "standardBlindInLast" : lookupTablePath({ "standard" : "自訂" }), "holeDiameter" : 3 * mm, "isTappedThrough" : true, "tappedDepth" : 12 * mm, "tapClearance" : 3, "locations" : qUnion([Q0, Q1]), "scope" : qUnion([Q2])});
        }
        {
            var Q0;
            Q0=makeQuery(id+"F33.boolean.opBoolean","MERGE",FACE,{"derivedFrom":[makeQuery(id+"F1.opExtrude","CAP_FACE",FACE,{"disambiguationData":[OSD([sQuery(id+"F0.wireOp",EDGE,"E0.bottom"),sQuery(id+"F0.wireOp",EDGE,"E0.top"),sQuery(id+"F0.wireOp",EDGE,"E0.left"),sQuery(id+"F0.wireOp",EDGE,"E0.right"),sQuery(id+"F0.wireOp",EDGE,"qFsGaKan-yORc-CTVH-xqod-amC7XaK1J5uG"),sQuery(id+"F0.wireOp",EDGE,"E1"),sQuery(id+"F0.wireOp",EDGE,"E2.MirrorCS"),sQuery(id+"F0.wireOp",EDGE,"cd217c19-c853-48cb-b8bd-9b78fb10cb74.filletArc"),sQuery(id+"F0.wireOp",EDGE,"a7c015ec-a513-4ea6-9d75-b2fe8166aac2.filletArc"),sQuery(id+"F0.wireOp",EDGE,"E3.filletArc"),sQuery(id+"F0.wireOp",EDGE,"E4.filletArc")])],"isStart":true}),makeQuery(id+"F33.opExtrude","SWEPT_FACE",FACE,{"disambiguationData":[OSD([sQuery(id+"F32.wireOp",EDGE,"E37.top")])]})]});
            var sketch = newSketch(context, id + "F37", { "sketchPlane" : qUnion([Q0])});
            skLineSegment(sketch, "E43.bottom", {"start": v(-51.79, -0.93) * mm, "end": v(-61.79, -0.93) * mm});
            skLineSegment(sketch, "E43.left", {"start": v(-51.79, -0.93) * mm, "end": v(-51.79, 11.57) * mm});
            skLineSegment(sketch, "E43.right", {"start": v(-61.79, -0.93) * mm, "end": v(-61.79, 11.57) * mm});
            skLineSegment(sketch, "E44", {"start": v(-61.79, 11.57) * mm, "end": v(-51.79, 11.57) * mm});
            skSolve(sketch);
        }
        {
            var Q0;
            Q0=qSketchRegion(id+"F37",true);
            extrude(context, id + "F38", {"entities" : qUnion([Q0]), "operationType" : NewBodyOperationType.REMOVE, "endBound" : BoundingType.THROUGH_ALL, "oppositeDirection" : true, "depth" : 25 * mm});
        }
        {
            var Q0;
            Q0=makeQuery(id+"F20.boolean.opBoolean","COPY",FACE,{"derivedFrom":makeQuery(id+"F20.opExtrude","SWEPT_FACE",FACE,{"disambiguationData":[OSD([sQuery(id+"F15.wireOp",EDGE,"E21")])]})});
            var sketch = newSketch(context, id + "F39", { "sketchPlane" : qUnion([Q0])});
            skLineSegment(sketch, "E45", {"start": v(-55.93, 0) * mm, "end": v(-55.93, 50) * mm});
            skLineSegment(sketch, "E46", {"start": v(-51.02, 0) * mm, "end": v(-51.02, 50) * mm});
            skCircle(sketch, "E47.cCircle", {"center": v(-55.93, 10) * mm, "radius": 3 * mm, "construction": true});
            skLineSegment(sketch, "E47.0", {"start": v(-52.93, 11.73) * mm, "end": v(-52.93, 8.27) * mm});
            skLineSegment(sketch, "E47.1", {"start": v(-52.93, 8.27) * mm, "end": v(-55.93, 6.54) * mm});
            skLineSegment(sketch, "E47.2", {"start": v(-55.93, 6.54) * mm, "end": v(-58.93, 8.27) * mm});
            skLineSegment(sketch, "E47.3", {"start": v(-58.93, 8.27) * mm, "end": v(-58.93, 11.73) * mm});
            skLineSegment(sketch, "E47.4", {"start": v(-58.93, 11.73) * mm, "end": v(-55.93, 13.46) * mm});
            skLineSegment(sketch, "E47.5", {"start": v(-55.93, 13.46) * mm, "end": v(-52.93, 11.73) * mm});
            skPoint(sketch, "E47.0.midPoint", {"position": v(-52.93, 10) * mm});
            skCircle(sketch, "E48.cCircle", {"center": v(-55.93, 40) * mm, "radius": 3 * mm, "construction": true});
            skLineSegment(sketch, "E48.0", {"start": v(-52.93, 41.73) * mm, "end": v(-52.93, 38.27) * mm});
            skLineSegment(sketch, "E48.1", {"start": v(-52.93, 38.27) * mm, "end": v(-55.93, 36.54) * mm});
            skLineSegment(sketch, "E48.2", {"start": v(-55.93, 36.54) * mm, "end": v(-58.93, 38.27) * mm});
            skLineSegment(sketch, "E48.3", {"start": v(-58.93, 38.27) * mm, "end": v(-58.93, 41.73) * mm});
            skLineSegment(sketch, "E48.4", {"start": v(-58.93, 41.73) * mm, "end": v(-55.93, 43.46) * mm});
            skLineSegment(sketch, "E48.5", {"start": v(-55.93, 43.46) * mm, "end": v(-52.93, 41.73) * mm});
            skPoint(sketch, "E48.0.midPoint", {"position": v(-52.93, 40) * mm});
            skSolve(sketch);
        }
        {
            var Q0;
            Q0=qSketchRegion(id+"F39",true);
            extrude(context, id + "F40", {"entities" : qUnion([Q0]), "operationType" : NewBodyOperationType.REMOVE, "oppositeDirection" : true, "depth" : 4 * mm});
        }
        {
            var Q0;
            Q0=sQuery(id+"F39.wireOp",VERTEX,"E47.cCircle.center");
            var Q1;
            Q1=sQuery(id+"F39.wireOp",VERTEX,"E48.cCircle.center");
            var Q2;
            Q2=makeQuery(id+"F1.opExtrude","SWEPT_BODY",BODY,{"disambiguationData":[OSD([sQuery(id+"F0.wireOp",EDGE,"E0.bottom"),sQuery(id+"F0.wireOp",EDGE,"E0.top"),sQuery(id+"F0.wireOp",EDGE,"E0.left"),sQuery(id+"F0.wireOp",EDGE,"E0.right"),sQuery(id+"F0.wireOp",EDGE,"qFsGaKan-yORc-CTVH-xqod-amC7XaK1J5uG"),sQuery(id+"F0.wireOp",EDGE,"E1"),sQuery(id+"F0.wireOp",EDGE,"E2.MirrorCS"),sQuery(id+"F0.wireOp",EDGE,"cd217c19-c853-48cb-b8bd-9b78fb10cb74.filletArc"),sQuery(id+"F0.wireOp",EDGE,"a7c015ec-a513-4ea6-9d75-b2fe8166aac2.filletArc"),sQuery(id+"F0.wireOp",EDGE,"E3.filletArc"),sQuery(id+"F0.wireOp",EDGE,"E4.filletArc")])]});
            hole(context, id + "F41", {"style" : HoleStyle.SIMPLE, "endStyle" : HoleEndStyle.THROUGH, "holeDiameter" : 3 * mm, "isTappedThrough" : true, "tappedDepth" : 12 * mm, "tapClearance" : 3, "locations" : qUnion([Q0, Q1]), "scope" : qUnion([Q2])});
        }
        {
            var Q0;
            {var subQ0=sQuery(id+"F32.wireOp",EDGE,"E40.right");Q0=makeQuery(id+"F32.imprint","IMPRINT",FACE,{"disambiguationData":[TD([[makeQuery(id+"F32.imprint","IMPRINT",EDGE,{"derivedFrom":subQ0}),1.0]])]});}
            extrude(context, id + "F42", {"entities" : qUnion([Q0]), "operationType" : NewBodyOperationType.REMOVE, "endBound" : BoundingType.THROUGH_ALL, "depth" : 25 * mm});
        }
        {
            var Q0;
            Q0=makeQuery(id+"F42.boolean.opBoolean","COPY",FACE,{"derivedFrom":makeQuery(id+"F42.opExtrude","CAP_FACE",FACE,{"disambiguationData":[OSD([sQuery(id+"F32.wireOp",EDGE,"E40.bottom"),sQuery(id+"F32.wireOp",EDGE,"E40.right"),sQuery(id+"F32.wireOp",EDGE,"E41"),sQuery(id+"F32.wireOp",EDGE,"SkDetiwh-NikU-a4By-Mc3j-X8Sh8EZGs6Av")])],"isStart":true})});
            extrude(context, id + "F43", {"entities" : qUnion([Q0]), "operationType" : NewBodyOperationType.REMOVE, "oppositeDirection" : true, "depth" : 10 * mm});
        }
        {
            var Q0;
            {var subQ0=sQuery(id+"F32.wireOp",EDGE,"E41");var subQ1=sQuery(id+"F32.wireOp",EDGE,"E40.right");Q0=makeQuery(id+"F43.boolean.opBoolean","MERGE",EDGE,{"derivedFrom":[makeQuery(id+"F42.boolean.opBoolean","COPY",EDGE,{"derivedFrom":makeQuery(id+"F42.opExtrude","SWEPT_EDGE",EDGE,{"disambiguationData":[OSD([subQ1,subQ0])]})}),makeQuery(id+"F43.opExtrude","SWEPT_EDGE",EDGE,{"disambiguationData":[OSD([subQ1,subQ0])]})]});}
            fillet(context, id + "F44", {"entities" : qUnion([Q0]), "radius" : 10 * mm, "tangentPropagation" : true, "allowEdgeOverflow" : false});
        }
        {
            var Q0;
            Q0=makeQuery(id+"F33.boolean.opBoolean","MERGE",FACE,{"derivedFrom":[makeQuery(id+"F26.boolean.opBoolean","COPY",FACE,{"derivedFrom":makeQuery(id+"F26.opExtrude","SWEPT_FACE",FACE,{"disambiguationData":[OSD([sQuery(id+"F22.wireOp",EDGE,"E33")])]})}),makeQuery(id+"F33.opExtrude","SWEPT_FACE",FACE,{"disambiguationData":[OSD([sQuery(id+"F32.wireOp",EDGE,"E39")])]})]});
            var sketch = newSketch(context, id + "F45", { "sketchPlane" : qUnion([Q0])});
            skCircle(sketch, "E49.cCircle", {"center": v(61.79, 45) * mm, "radius": 3 * mm, "construction": true});
            skLineSegment(sketch, "E49.0", {"start": v(58.79, 43.27) * mm, "end": v(58.79, 46.73) * mm});
            skLineSegment(sketch, "E49.1", {"start": v(58.79, 46.73) * mm, "end": v(61.79, 48.46) * mm});
            skLineSegment(sketch, "E49.2", {"start": v(61.79, 48.46) * mm, "end": v(64.79, 46.73) * mm});
            skLineSegment(sketch, "E49.3", {"start": v(64.79, 46.73) * mm, "end": v(64.79, 43.27) * mm});
            skLineSegment(sketch, "E49.4", {"start": v(64.79, 43.27) * mm, "end": v(61.79, 41.54) * mm});
            skLineSegment(sketch, "E49.5", {"start": v(61.79, 41.54) * mm, "end": v(58.79, 43.27) * mm});
            skPoint(sketch, "E49.0.midPoint", {"position": v(58.79, 45) * mm});
            skLineSegment(sketch, "E50", {"start": v(61.79, 45) * mm, "end": v(41.7, 45) * mm});
            skCircle(sketch, "E51.cCircle", {"center": v(46.79, 45) * mm, "radius": 3 * mm, "construction": true});
            skLineSegment(sketch, "E51.0", {"start": v(49.79, 46.73) * mm, "end": v(49.79, 43.27) * mm});
            skLineSegment(sketch, "E51.1", {"start": v(49.79, 43.27) * mm, "end": v(46.79, 41.54) * mm});
            skLineSegment(sketch, "E51.2", {"start": v(46.79, 41.54) * mm, "end": v(43.79, 43.27) * mm});
            skLineSegment(sketch, "E51.3", {"start": v(43.79, 43.27) * mm, "end": v(43.79, 46.73) * mm});
            skLineSegment(sketch, "E51.4", {"start": v(43.79, 46.73) * mm, "end": v(46.79, 48.46) * mm});
            skLineSegment(sketch, "E51.5", {"start": v(46.79, 48.46) * mm, "end": v(49.79, 46.73) * mm});
            skPoint(sketch, "E51.0.midPoint", {"position": v(49.79, 45) * mm});
            skSolve(sketch);
        }
        {
            var Q0;
            Q0=qSketchRegion(id+"F45",true);
            extrude(context, id + "F46", {"entities" : qUnion([Q0]), "operationType" : NewBodyOperationType.REMOVE, "oppositeDirection" : true, "depth" : 4 * mm});
        }
        {
            var Q0;
            Q0=makeQuery(id+"F35.boolean.opBoolean","INTERSECT",EDGE,{"derivedFrom":[makeQuery(id+"F33.opExtrude","CAP_FACE",FACE,{"disambiguationData":[OSD([sQuery(id+"F32.wireOp",EDGE,"E37.bottom"),sQuery(id+"F32.wireOp",EDGE,"E37.top"),sQuery(id+"F32.wireOp",EDGE,"E37.left"),sQuery(id+"F32.wireOp",EDGE,"E37.right"),sQuery(id+"F32.wireOp",EDGE,"E38"),sQuery(id+"F32.wireOp",EDGE,"E39"),sQuery(id+"F32.wireOp",EDGE,"E40.bottom"),sQuery(id+"F32.wireOp",EDGE,"E40.left")])],"isStart":false}),makeQuery(id+"F35.opExtrude","SWEPT_FACE",FACE,{"disambiguationData":[OSD([sQuery(id+"F0.wireOp",EDGE,"E0.left"),sQuery(id+"F22.wireOp",EDGE,"E32")])]})]});
            var Q1;
            Q1=makeQuery(id+"F29.boolean.opBoolean","COPY",EDGE,{"derivedFrom":makeQuery(id+"F29.opExtrude","CAP_EDGE",EDGE,{"disambiguationData":[OSD([sQuery(id+"F22.wireOp",EDGE,"E28")])],"isStart":true})});
            var Q2;
            Q2=makeQuery(id+"F29.boolean.opBoolean","COPY",EDGE,{"derivedFrom":makeQuery(id+"F29.opExtrude","CAP_EDGE",EDGE,{"disambiguationData":[OSD([sQuery(id+"F22.wireOp",EDGE,"E32")])],"isStart":false})});
            var Q3;
            Q3=makeQuery(id+"F31.boolean.opBoolean","COPY",EDGE,{"derivedFrom":makeQuery(id+"F31.opExtrude","CAP_EDGE",EDGE,{"disambiguationData":[OSD([sQuery(id+"F0.wireOp",EDGE,"E0.left"),sQuery(id+"F22.wireOp",EDGE,"E32")])],"isStart":false})});
            var Q4;
            Q4=makeQuery(id+"F34.boolean.opBoolean","INTERSECT",EDGE,{"derivedFrom":[makeQuery(id+"F33.opExtrude","CAP_FACE",FACE,{"disambiguationData":[OSD([sQuery(id+"F32.wireOp",EDGE,"E37.bottom"),sQuery(id+"F32.wireOp",EDGE,"E37.top"),sQuery(id+"F32.wireOp",EDGE,"E37.left"),sQuery(id+"F32.wireOp",EDGE,"E37.right"),sQuery(id+"F32.wireOp",EDGE,"E38"),sQuery(id+"F32.wireOp",EDGE,"E39"),sQuery(id+"F32.wireOp",EDGE,"E40.bottom"),sQuery(id+"F32.wireOp",EDGE,"E40.left")])],"isStart":true}),makeQuery(id+"F34.opExtrude","SWEPT_FACE",FACE,{"disambiguationData":[OSD([sQuery(id+"F22.wireOp",EDGE,"E28")])]})]});
            var Q5;
            Q5=makeQuery(id+"F34.boolean.opBoolean","COPY",EDGE,{"derivedFrom":makeQuery(id+"F34.opExtrude","CAP_EDGE",EDGE,{"disambiguationData":[OSD([sQuery(id+"F22.wireOp",EDGE,"E32")])],"isStart":false})});
            fillet(context, id + "F47", {"entities" : qUnion([Q0, Q1, Q2, Q3, Q4, Q5]), "radius" : 1 * mm, "tangentPropagation" : true, "allowEdgeOverflow" : false});
        }
        {
            var Q0;
            Q0=makeQuery(id+"F20.boolean.opBoolean","COPY",EDGE,{"derivedFrom":makeQuery(id+"F20.opExtrude","CAP_EDGE",EDGE,{"disambiguationData":[OSD([sQuery(id+"F15.wireOp",EDGE,"E21")])],"isStart":true})});
            var Q1;
            Q1=makeQuery(id+"F1.opExtrude","SWEPT_EDGE",EDGE,{"disambiguationData":[OSD([sQuery(id+"F0.wireOp",EDGE,"E0.bottom"),sQuery(id+"F0.wireOp",EDGE,"E0.right")])]});
            var Q2;
            Q2=makeQuery(id+"F26.boolean.opBoolean","COPY",EDGE,{"derivedFrom":makeQuery(id+"F26.opExtrude","CAP_EDGE",EDGE,{"disambiguationData":[OSD([sQuery(id+"F22.wireOp",EDGE,"E31"),sQuery(id+"F22.wireOp",EDGE,"E35")])],"isStart":true})});
            var Q3;
            Q3=makeQuery(id+"F20.boolean.opBoolean","INTERSECT",EDGE,{"derivedFrom":[makeQuery(id+"F16.hole-0.boolean.opBoolean","COPY",FACE,{"derivedFrom":makeQuery(id+"F16.hole-0.opRevolve","SWEPT_FACE",FACE,{"disambiguationData":[OSD([sQuery(id+"F16.hole-0.sketch.wireOp",EDGE,"core_line_2")])]})}),makeQuery(id+"F20.opExtrude","CAP_FACE",FACE,{"disambiguationData":[OSD([sQuery(id+"F0.wireOp",EDGE,"E0.bottom"),sQuery(id+"F0.wireOp",EDGE,"E0.left"),sQuery(id+"F15.wireOp",EDGE,"E18"),sQuery(id+"F15.wireOp",EDGE,"E19"),sQuery(id+"F15.wireOp",EDGE,"E20.MirrorCS"),sQuery(id+"F15.wireOp",EDGE,"E21"),sQuery(id+"F15.wireOp",EDGE,"E22.bottom")])],"isStart":false})]});
            var Q4;
            Q4=makeQuery(id+"F20.boolean.opBoolean","COPY",EDGE,{"derivedFrom":makeQuery(id+"F20.opExtrude","CAP_EDGE",EDGE,{"disambiguationData":[OSD([sQuery(id+"F15.wireOp",EDGE,"E19")])],"isStart":false})});
            var Q5;
            Q5=makeQuery(id+"F20.boolean.opBoolean","COPY",EDGE,{"derivedFrom":makeQuery(id+"F20.opExtrude","CAP_EDGE",EDGE,{"disambiguationData":[OSD([sQuery(id+"F15.wireOp",EDGE,"E20.MirrorCS")])],"isStart":false})});
            var Q6;
            Q6=makeQuery(id+"F16.hole-0.boolean.opBoolean","INTERSECT",EDGE,{"derivedFrom":[makeQuery(id+"F1.opExtrude","SWEPT_FACE",FACE,{"disambiguationData":[OSD([sQuery(id+"F0.wireOp",EDGE,"E0.top")])]}),makeQuery(id+"F16.hole-0.opRevolve","SWEPT_FACE",FACE,{"disambiguationData":[OSD([sQuery(id+"F16.hole-0.sketch.wireOp",EDGE,"core_line_2")])]})]});
            var Q7;
            Q7=makeQuery(id+"FFivbzgTC0pYUuN_1.hole-0.boolean.opBoolean","INTERSECT",EDGE,{"derivedFrom":[makeQuery(id+"F33.boolean.opBoolean","MERGE",FACE,{"derivedFrom":[makeQuery(id+"F1.opExtrude","SWEPT_FACE",FACE,{"disambiguationData":[OSD([sQuery(id+"F0.wireOp",EDGE,"E0.top")])]}),makeQuery(id+"F33.opExtrude","SWEPT_FACE",FACE,{"disambiguationData":[OSD([sQuery(id+"F32.wireOp",EDGE,"E37.right")])]})]}),makeQuery(id+"FFivbzgTC0pYUuN_1.hole-0.opRevolve","SWEPT_FACE",FACE,{"disambiguationData":[OSD([sQuery(id+"FFivbzgTC0pYUuN_1.hole-0.sketch.wireOp",EDGE,"core_line_2")])]})]});
            var Q8;
            Q8=makeQuery(id+"FVzmiarrmhLZRJT_1.hole-0.boolean.opBoolean","INTERSECT",EDGE,{"derivedFrom":[makeQuery(id+"F33.boolean.opBoolean","MERGE",FACE,{"derivedFrom":[makeQuery(id+"F1.opExtrude","SWEPT_FACE",FACE,{"disambiguationData":[OSD([sQuery(id+"F0.wireOp",EDGE,"E0.top")])]}),makeQuery(id+"F33.opExtrude","SWEPT_FACE",FACE,{"disambiguationData":[OSD([sQuery(id+"F32.wireOp",EDGE,"E37.right")])]})]}),makeQuery(id+"FVzmiarrmhLZRJT_1.hole-0.opRevolve","SWEPT_FACE",FACE,{"disambiguationData":[OSD([sQuery(id+"FVzmiarrmhLZRJT_1.hole-0.sketch.wireOp",EDGE,"core_line_2")])]})]});
            var Q9;
            Q9=makeQuery(id+"F6.opBoolean","INTERSECT",EDGE,{"derivedFrom":[makeQuery(id+"F1.opExtrude","SWEPT_FACE",FACE,{"disambiguationData":[OSD([sQuery(id+"F0.wireOp",EDGE,"E0.right")])]}),makeQuery(id+"F5.opExtrude","SWEPT_FACE",FACE,{"disambiguationData":[OSD([sQuery(id+"F2.wireOp",EDGE,"E11")])]})]});
            var Q10;
            Q10=makeQuery(id+"F12.hole-0.boolean.opBoolean","INTERSECT",EDGE,{"derivedFrom":[makeQuery(id+"F1.opExtrude","SWEPT_FACE",FACE,{"disambiguationData":[OSD([sQuery(id+"F0.wireOp",EDGE,"E0.right")])]}),makeQuery(id+"F12.hole-0.opRevolve","SWEPT_FACE",FACE,{"disambiguationData":[OSD([sQuery(id+"F12.hole-0.sketch.wireOp",EDGE,"core_line_2")])]})]});
            var Q11;
            Q11=makeQuery(id+"F41.hole-1.boolean.opBoolean","INTERSECT",EDGE,{"derivedFrom":[makeQuery(id+"F1.opExtrude","SWEPT_FACE",FACE,{"disambiguationData":[OSD([sQuery(id+"F0.wireOp",EDGE,"E0.right")])]}),makeQuery(id+"F41.hole-1.opRevolve","SWEPT_FACE",FACE,{"disambiguationData":[OSD([sQuery(id+"F41.hole-1.sketch.wireOp",EDGE,"core_line_2")])]})]});
            var Q12;
            Q12=makeQuery(id+"F41.hole-0.boolean.opBoolean","INTERSECT",EDGE,{"derivedFrom":[makeQuery(id+"F1.opExtrude","SWEPT_FACE",FACE,{"disambiguationData":[OSD([sQuery(id+"F0.wireOp",EDGE,"E0.right")])]}),makeQuery(id+"F41.hole-0.opRevolve","SWEPT_FACE",FACE,{"disambiguationData":[OSD([sQuery(id+"F41.hole-0.sketch.wireOp",EDGE,"core_line_2")])]})]});
            fillet(context, id + "F48", {"entities" : qUnion([Q0, Q1, Q2, Q3, Q4, Q5, Q6, Q7, Q8, Q9, Q10, Q11, Q12]), "radius" : 1 * mm, "tangentPropagation" : true, "allowEdgeOverflow" : false});
        }
        {
            var Q0;
            Q0=makeQuery(id+"F10.boolean.opBoolean","INTERSECT",EDGE,{"derivedFrom":[makeQuery(id+"F1.opExtrude","SWEPT_FACE",FACE,{"disambiguationData":[OSD([sQuery(id+"F0.wireOp",EDGE,"E0.top")])]}),makeQuery(id+"F10.opExtrude","SWEPT_FACE",FACE,{"disambiguationData":[OSD([sQuery(id+"F9.wireOp",EDGE,"E17.3")])]})]});
            var Q1;
            Q1=makeQuery(id+"F10.boolean.opBoolean","INTERSECT",EDGE,{"derivedFrom":[makeQuery(id+"F1.opExtrude","SWEPT_FACE",FACE,{"disambiguationData":[OSD([sQuery(id+"F0.wireOp",EDGE,"E0.top")])]}),makeQuery(id+"F10.opExtrude","SWEPT_FACE",FACE,{"disambiguationData":[OSD([sQuery(id+"F9.wireOp",EDGE,"E15.5")])]})]});
            chamfer(context, id + "F49", {"entities" : qUnion([Q0, Q1]), "width" : 1 * mm, "tangentPropagation" : true});
        }
        {
            var Q0;
            Q0=makeQuery(id+"F33.opExtrude","CAP_EDGE",EDGE,{"disambiguationData":[OSD([sQuery(id+"F32.wireOp",EDGE,"E37.left"),sQuery(id+"F32.wireOp",EDGE,"E40.left")])],"isStart":true});
            var Q1;
            Q1=makeQuery(id+"F33.opExtrude","CAP_EDGE",EDGE,{"disambiguationData":[OSD([sQuery(id+"F32.wireOp",EDGE,"E37.left"),sQuery(id+"F32.wireOp",EDGE,"E40.left")])],"isStart":false});
            var Q2;
            Q2=makeQuery(id+"F33.opExtrude","CAP_EDGE",EDGE,{"disambiguationData":[OSD([sQuery(id+"F32.wireOp",EDGE,"E37.right")])],"isStart":false});
            fillet(context, id + "F50", {"entities" : qUnion([Q0, Q1, Q2]), "radius" : 1 * mm, "tangentPropagation" : true, "allowEdgeOverflow" : false});
        }
        {
            var Q0;
            Q0=makeQuery(id+"F33.opExtrude","SWEPT_EDGE",EDGE,{"disambiguationData":[OSD([sQuery(id+"F32.wireOp",EDGE,"E37.left"),sQuery(id+"F32.wireOp",EDGE,"E38")])]});
            fillet(context, id + "F51", {"entities" : qUnion([Q0]), "radius" : 1 * mm, "tangentPropagation" : true, "allowEdgeOverflow" : false});
        }
        {
            var Q0;
            Q0=makeQuery(id+"F20.boolean.opBoolean","COPY",EDGE,{"derivedFrom":makeQuery(id+"F20.opExtrude","CAP_EDGE",EDGE,{"disambiguationData":[OSD([sQuery(id+"F15.wireOp",EDGE,"E21")])],"isStart":false})});
            fillet(context, id + "F52", {"entities" : qUnion([Q0]), "radius" : 5 * mm, "tangentPropagation" : true, "allowEdgeOverflow" : false});
        }
        {
            var Q0;
            Q0=sQuery(id+"F45.wireOp",VERTEX,"E50.start");
            var Q1;
            Q1=sQuery(id+"F45.wireOp",VERTEX,"E51.cCircle.center");
            var Q2;
            Q2=makeQuery(id+"F1.opExtrude","SWEPT_BODY",BODY,{"disambiguationData":[OSD([sQuery(id+"F0.wireOp",EDGE,"E0.bottom"),sQuery(id+"F0.wireOp",EDGE,"E0.top"),sQuery(id+"F0.wireOp",EDGE,"E0.left"),sQuery(id+"F0.wireOp",EDGE,"E0.right"),sQuery(id+"F0.wireOp",EDGE,"qFsGaKan-yORc-CTVH-xqod-amC7XaK1J5uG"),sQuery(id+"F0.wireOp",EDGE,"E1"),sQuery(id+"F0.wireOp",EDGE,"E2.MirrorCS"),sQuery(id+"F0.wireOp",EDGE,"cd217c19-c853-48cb-b8bd-9b78fb10cb74.filletArc"),sQuery(id+"F0.wireOp",EDGE,"a7c015ec-a513-4ea6-9d75-b2fe8166aac2.filletArc"),sQuery(id+"F0.wireOp",EDGE,"E3.filletArc"),sQuery(id+"F0.wireOp",EDGE,"E4.filletArc")])]});
            hole(context, id + "F53", {"style" : HoleStyle.SIMPLE, "endStyle" : HoleEndStyle.THROUGH, "holeDiameter" : 3 * mm, "isTappedThrough" : true, "tappedDepth" : 12 * mm, "tapClearance" : 3, "locations" : qUnion([Q0, Q1]), "scope" : qUnion([Q2])});
        }
        {
            var Q0;
            Q0=makeQuery(id+"F33.boolean.opBoolean","MERGE",FACE,{"derivedFrom":[makeQuery(id+"F1.opExtrude","CAP_FACE",FACE,{"disambiguationData":[OSD([sQuery(id+"F0.wireOp",EDGE,"E0.bottom"),sQuery(id+"F0.wireOp",EDGE,"E0.top"),sQuery(id+"F0.wireOp",EDGE,"E0.left"),sQuery(id+"F0.wireOp",EDGE,"E0.right"),sQuery(id+"F0.wireOp",EDGE,"qFsGaKan-yORc-CTVH-xqod-amC7XaK1J5uG"),sQuery(id+"F0.wireOp",EDGE,"E1"),sQuery(id+"F0.wireOp",EDGE,"E2.MirrorCS"),sQuery(id+"F0.wireOp",EDGE,"cd217c19-c853-48cb-b8bd-9b78fb10cb74.filletArc"),sQuery(id+"F0.wireOp",EDGE,"a7c015ec-a513-4ea6-9d75-b2fe8166aac2.filletArc"),sQuery(id+"F0.wireOp",EDGE,"E3.filletArc"),sQuery(id+"F0.wireOp",EDGE,"E4.filletArc")])],"isStart":false}),makeQuery(id+"F33.opExtrude","SWEPT_FACE",FACE,{"disambiguationData":[OSD([sQuery(id+"F32.wireOp",EDGE,"E37.bottom")])]})]});
            var sketch = newSketch(context, id + "F54", { "sketchPlane" : qUnion([Q0])});
            skLineSegment(sketch, "E52.bottom", {"start": v(-6.99, 60.93) * mm, "end": v(-4.79, 60.93) * mm});
            skLineSegment(sketch, "E52.top", {"start": v(-6.99, 57.93) * mm, "end": v(-4.79, 57.93) * mm});
            skLineSegment(sketch, "E52.left", {"start": v(-6.99, 60.93) * mm, "end": v(-6.99, 57.93) * mm});
            skLineSegment(sketch, "E52.right", {"start": v(-4.79, 60.93) * mm, "end": v(-4.79, 57.93) * mm});
            skLineSegment(sketch, "E53.bottom", {"start": v(-71.79, 6.13) * mm, "end": v(-68.79, 6.13) * mm});
            skLineSegment(sketch, "E53.top", {"start": v(-71.79, 3.93) * mm, "end": v(-68.79, 3.93) * mm});
            skLineSegment(sketch, "E53.left", {"start": v(-71.79, 6.13) * mm, "end": v(-71.79, 3.93) * mm});
            skLineSegment(sketch, "E53.right", {"start": v(-68.79, 6.13) * mm, "end": v(-68.79, 3.93) * mm});
            skSolve(sketch);
        }
        {
            var Q0;
            Q0=makeQuery(id+"F54.imprint","IMPRINT",FACE,{"disambiguationData":[TD([[makeQuery(id+"F54.imprint","IMPRINT",EDGE,{"derivedFrom":sQuery(id+"F54.wireOp",EDGE,"E53.bottom")}),-1.0]])]});
            var Q1;
            Q1=makeQuery(id+"F54.imprint","IMPRINT",FACE,{"disambiguationData":[TD([[makeQuery(id+"F54.imprint","IMPRINT",EDGE,{"derivedFrom":sQuery(id+"F54.wireOp",EDGE,"E52.bottom")}),-1.0]])]});
            extrude(context, id + "F55", {"entities" : qUnion([Q0, Q1]), "operationType" : NewBodyOperationType.REMOVE, "endBound" : BoundingType.THROUGH_ALL, "oppositeDirection" : true, "depth" : 25 * mm});
        }
        {
            var Q0;
            Q0=makeQuery(id+"F1.opExtrude","SWEPT_EDGE",EDGE,{"disambiguationData":[OSD([sQuery(id+"F0.wireOp",EDGE,"E7"),sQuery(id+"F0.wireOp",EDGE,"E8")])]});
            var Q1;
            Q1=makeQuery(id+"F1.opExtrude","SWEPT_EDGE",EDGE,{"disambiguationData":[OSD([sQuery(id+"F0.wireOp",EDGE,"E6"),sQuery(id+"F0.wireOp",EDGE,"E9")])]});
            fillet(context, id + "F56", {"entities" : qUnion([Q0, Q1]), "radius" : 2 * mm, "tangentPropagation" : true, "allowEdgeOverflow" : false});
        }
    });
